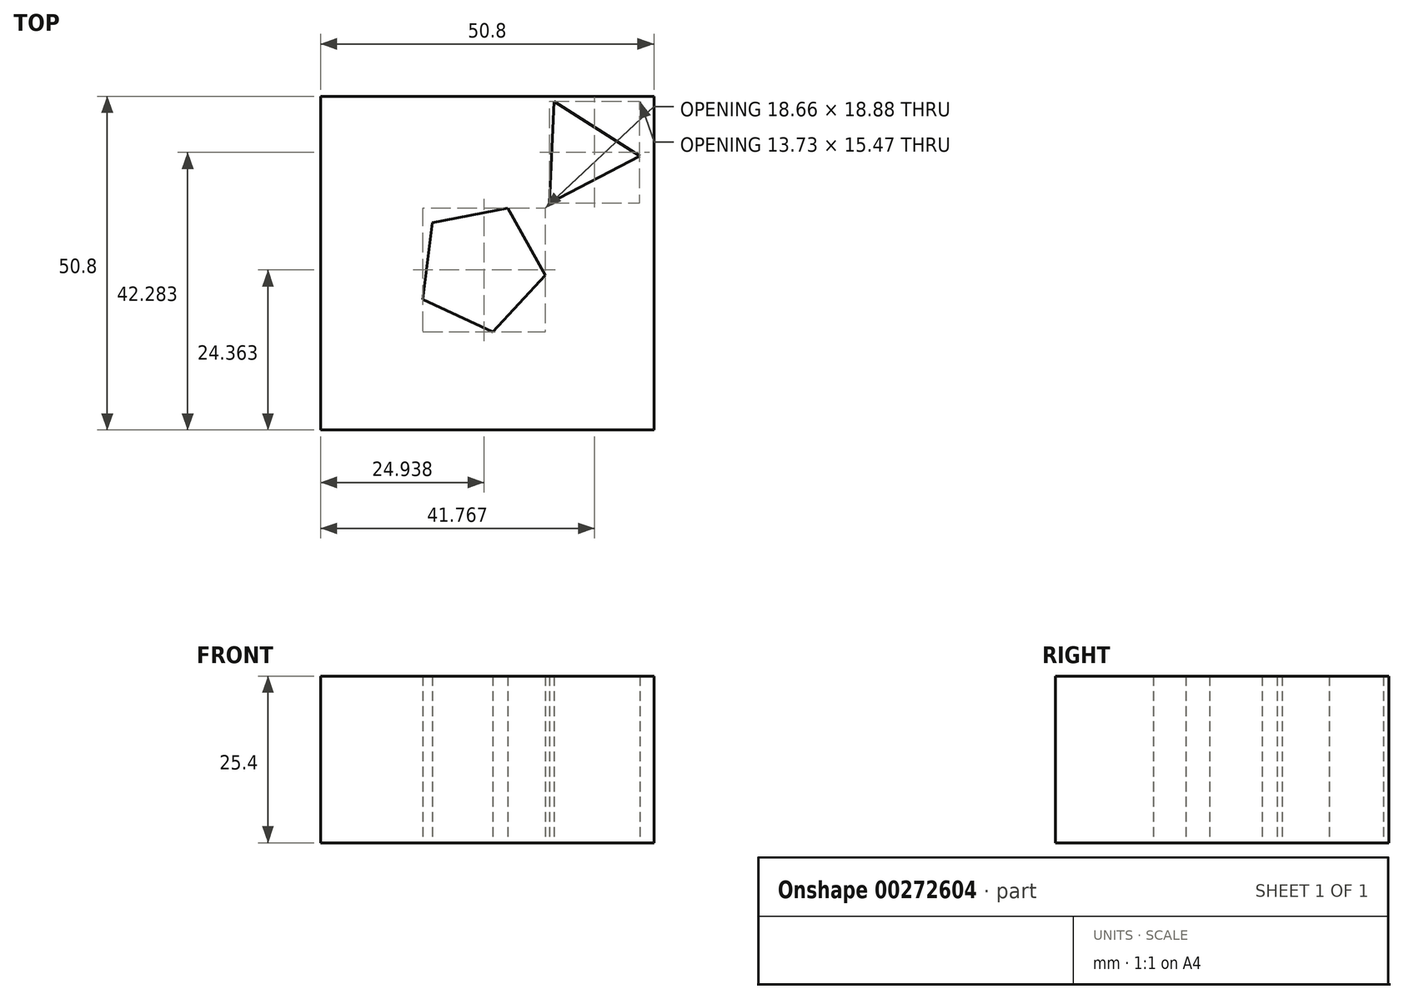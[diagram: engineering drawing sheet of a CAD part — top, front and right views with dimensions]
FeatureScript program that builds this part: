
annotation { "Feature Type Name" : "Feature", "Feature Type Description" : "" }
export const myFeature = defineFeature(function(context is Context, id is Id, definition is map)
    precondition{}
    {
        {
            var Q0;
            Q0=qCreatedBy(makeId("Top.planeOp"),FACE);
            var sketch = newSketch(context, id + "F0", { "sketchPlane" : qUnion([Q0])});
            skLineSegment(sketch, "E0.bottom", {"start": v(0, 8.7) * mm, "end": v(50.8, 8.7) * mm});
            skLineSegment(sketch, "E0.top", {"start": v(0, -42.1) * mm, "end": v(50.8, -42.1) * mm});
            skLineSegment(sketch, "E0.left", {"start": v(0, 8.7) * mm, "end": v(0, -42.1) * mm});
            skLineSegment(sketch, "E0.right", {"start": v(50.8, 8.7) * mm, "end": v(50.8, -42.1) * mm});
            skCircle(sketch, "E1.cCircle", {"center": v(24.34, -17.36) * mm, "radius": 8.09 * mm, "construction": true});
            skLineSegment(sketch, "E1.0", {"start": v(34.27, -18.55) * mm, "end": v(26.27, -27.17) * mm});
            skLineSegment(sketch, "E1.1", {"start": v(26.27, -27.17) * mm, "end": v(15.6, -22.22) * mm});
            skLineSegment(sketch, "E1.2", {"start": v(15.6, -22.22) * mm, "end": v(17.02, -10.55) * mm});
            skLineSegment(sketch, "E1.3", {"start": v(17.02, -10.55) * mm, "end": v(28.55, -8.29) * mm});
            skLineSegment(sketch, "E1.4", {"start": v(28.55, -8.29) * mm, "end": v(34.27, -18.55) * mm});
            skPoint(sketch, "E1.0.midPoint", {"position": v(30.27, -22.86) * mm});
            skCircle(sketch, "E2.cCircle", {"center": v(39.7, 0) * mm, "radius": 4.47 * mm, "construction": true});
            skLineSegment(sketch, "E2.0", {"start": v(48.63, -0.39) * mm, "end": v(34.9, -7.54) * mm});
            skLineSegment(sketch, "E2.1", {"start": v(34.9, -7.54) * mm, "end": v(35.57, 7.93) * mm});
            skLineSegment(sketch, "E2.2", {"start": v(35.57, 7.93) * mm, "end": v(48.63, -0.39) * mm});
            skPoint(sketch, "E2.0.midPoint", {"position": v(41.77, -3.96) * mm});
            skSolve(sketch);
        }
        {
            var Q0;
            Q0 = qSketchRegion(id + "F0", true);
            var Q1;
            Q1=makeQuery(id+"F0.imprint","IMPRINT",FACE,{"disambiguationData":[TD([[makeQuery(id+"F0.imprint","IMPRINT",EDGE,{"derivedFrom":sQuery(id+"F0.wireOp",EDGE,"579e6e1d-b59b-4924-a08e-9ddae13f5ba9.0")}),-1.0]])]});
            extrude(context, id + "F1", {"entities" : qUnion([Q0, Q1]), "depth" : 25.4 * mm});
        }
        {
            var Q0;
            Q0 = qSketchRegion(id + "F0", true);
            extrude(context, id + "F2", {"entities" : qUnion([Q0]), "operationType" : NewBodyOperationType.ADD, "depth" : 25.4 * mm});
        }
    });
